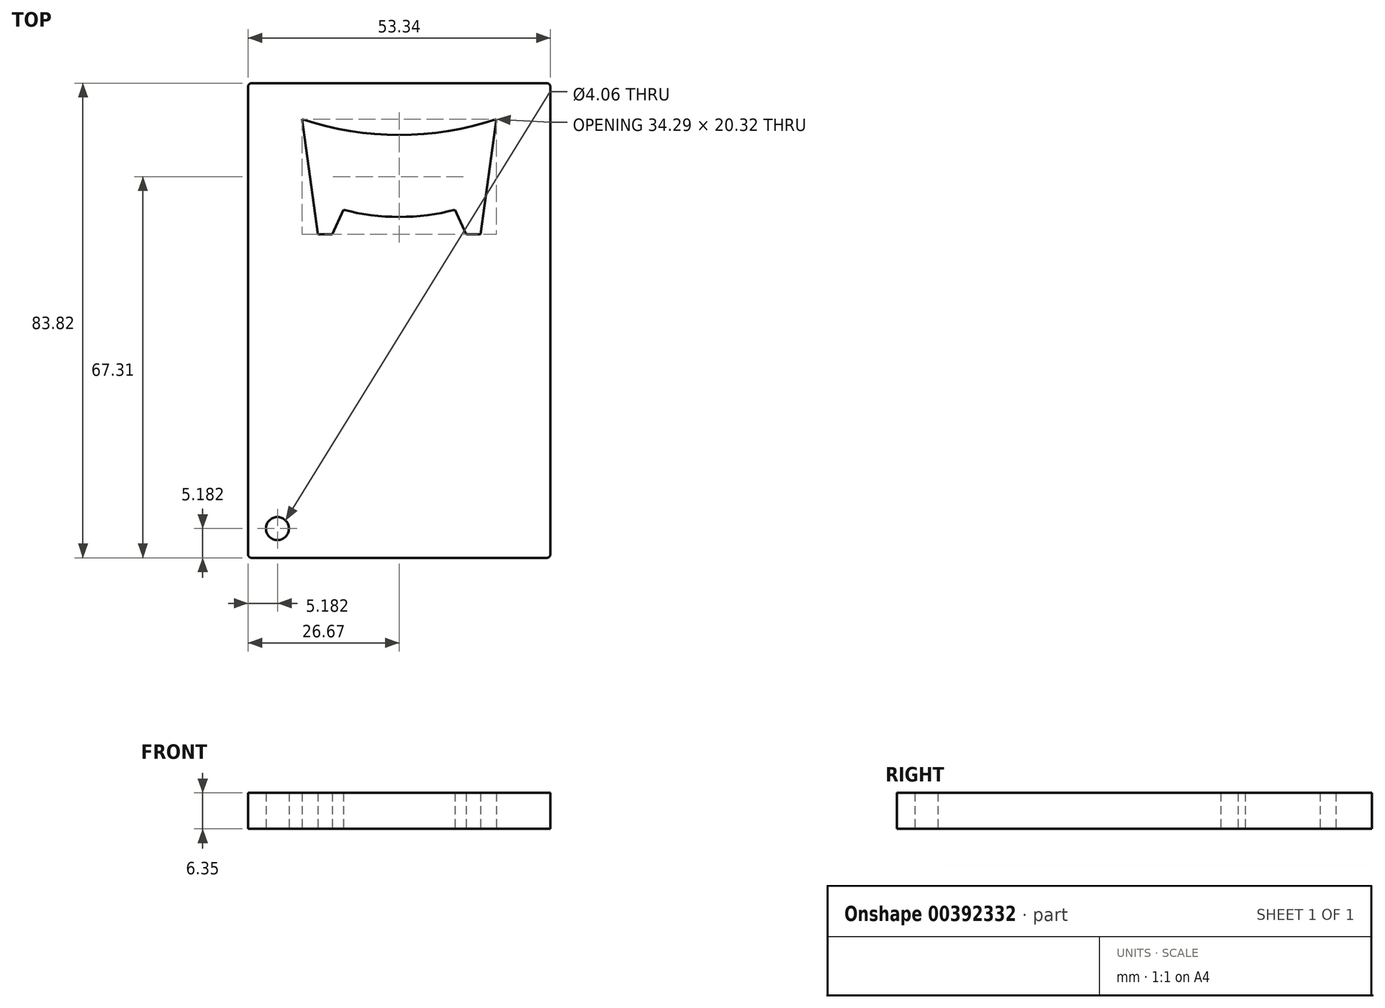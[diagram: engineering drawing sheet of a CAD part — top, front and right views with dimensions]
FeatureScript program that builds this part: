
annotation { "Feature Type Name" : "Feature", "Feature Type Description" : "" }
export const myFeature = defineFeature(function(context is Context, id is Id, definition is map)
    precondition{}
    {
        {
            var Q0;
            Q0=qCreatedBy(makeId("Top.planeOp"),FACE);
            var sketch = newSketch(context, id + "F0", { "sketchPlane" : qUnion([Q0])});
            skLineSegment(sketch, "E0.bottom", {"start": v(0.63, 0) * mm, "end": v(52.7, 0) * mm});
            skLineSegment(sketch, "E0.top", {"start": v(0.64, -83.82) * mm, "end": v(52.7, -83.82) * mm});
            skLineSegment(sketch, "E0.left", {"start": v(0, -0.64) * mm, "end": v(0, -83.19) * mm});
            skLineSegment(sketch, "E0.right", {"start": v(53.34, -0.64) * mm, "end": v(53.34, -83.19) * mm});
            skCircle(sketch, "E1", {"center": v(5.18, -78.64) * mm, "radius": 2.03 * mm});
            skLineSegment(sketch, "E2", {"start": v(0, -80.67) * mm, "end": v(5.18, -80.67) * mm, "construction": true});
            skLineSegment(sketch, "E3", {"start": v(3.15, -83.82) * mm, "end": v(3.15, -78.64) * mm, "construction": true});
            skLineSegment(sketch, "E4.bottom", {"start": v(9.52, -6.35) * mm, "end": v(43.82, -6.35) * mm, "construction": true});
            skLineSegment(sketch, "E4.top", {"start": v(9.52, -26.67) * mm, "end": v(43.82, -26.67) * mm, "construction": true});
            skLineSegment(sketch, "E4.left", {"start": v(9.52, -6.35) * mm, "end": v(9.52, -26.67) * mm, "construction": true});
            skLineSegment(sketch, "E4.right", {"start": v(43.82, -6.35) * mm, "end": v(43.82, -26.67) * mm, "construction": true});
            skLineSegment(sketch, "E5", {"start": v(43.82, -6.35) * mm, "end": v(41.02, -26.67) * mm, "construction": true});
            skLineSegment(sketch, "E6", {"start": v(9.52, -6.35) * mm, "end": v(12.32, -26.67) * mm, "construction": true});
            skLineSegment(sketch, "E7", {"start": v(26.67, -6.35) * mm, "end": v(26.67, -9.14) * mm, "construction": true});
            skArc(sketch, "E8", {"start": v(9.53, -6.35) * mm, "mid": v(26.67, -9.14) * mm, "end": v(43.82, -6.35) * mm});
            skLineSegment(sketch, "E9", {"start": v(9.52, -6.35) * mm, "end": v(12.32, -26.67) * mm});
            skLineSegment(sketch, "E10", {"start": v(43.82, -6.35) * mm, "end": v(41.02, -26.67) * mm});
            skLineSegment(sketch, "E11", {"start": v(12.32, -26.67) * mm, "end": v(14.86, -26.67) * mm});
            skLineSegment(sketch, "E12", {"start": v(41.02, -26.67) * mm, "end": v(38.48, -26.67) * mm});
            skLineSegment(sketch, "E13", {"start": v(38.48, -26.67) * mm, "end": v(36.53, -22.35) * mm});
            skLineSegment(sketch, "E14", {"start": v(14.86, -26.67) * mm, "end": v(16.8, -22.35) * mm});
            skLineSegment(sketch, "E15", {"start": v(11.73, -22.35) * mm, "end": v(41.61, -22.35) * mm, "construction": true});
            skLineSegment(sketch, "E16", {"start": v(26.67, -22.35) * mm, "end": v(26.67, -23.62) * mm, "construction": true});
            skArc(sketch, "E17", {"start": v(16.8, -22.35) * mm, "mid": v(26.67, -23.62) * mm, "end": v(36.53, -22.35) * mm});
            skPoint(sketch, "E18.visualSharp", {"position": v(0, 0) * mm});
            skArc(sketch, "E18.filletArc", {"start": v(0.63, 0) * mm, "mid": v(0.19, -0.19) * mm, "end": v(0, -0.64) * mm});
            skPoint(sketch, "E19.visualSharp", {"position": v(53.34, 0) * mm});
            skArc(sketch, "E19.filletArc", {"start": v(53.34, -0.64) * mm, "mid": v(53.15, -0.19) * mm, "end": v(52.7, 0) * mm});
            skPoint(sketch, "E20.visualSharp", {"position": v(0, -83.82) * mm});
            skArc(sketch, "E20.filletArc", {"start": v(0, -83.19) * mm, "mid": v(0.19, -83.63) * mm, "end": v(0.64, -83.82) * mm});
            skPoint(sketch, "E21.visualSharp", {"position": v(53.34, -83.82) * mm});
            skArc(sketch, "E21.filletArc", {"start": v(52.7, -83.82) * mm, "mid": v(53.15, -83.63) * mm, "end": v(53.34, -83.19) * mm});
            skSolve(sketch);
        }
        {
            var Q0;
            Q0=makeQuery(id+"F0.imprint","IMPRINT",FACE,{"disambiguationData":[TD([[makeQuery(id+"F0.imprint","IMPRINT",EDGE,{"derivedFrom":sQuery(id+"F0.wireOp",EDGE,"E0.bottom")}),-1.0]])]});
            extrude(context, id + "F1", {"entities" : qUnion([Q0]), "depth" : 6.35 * mm});
        }
    });
